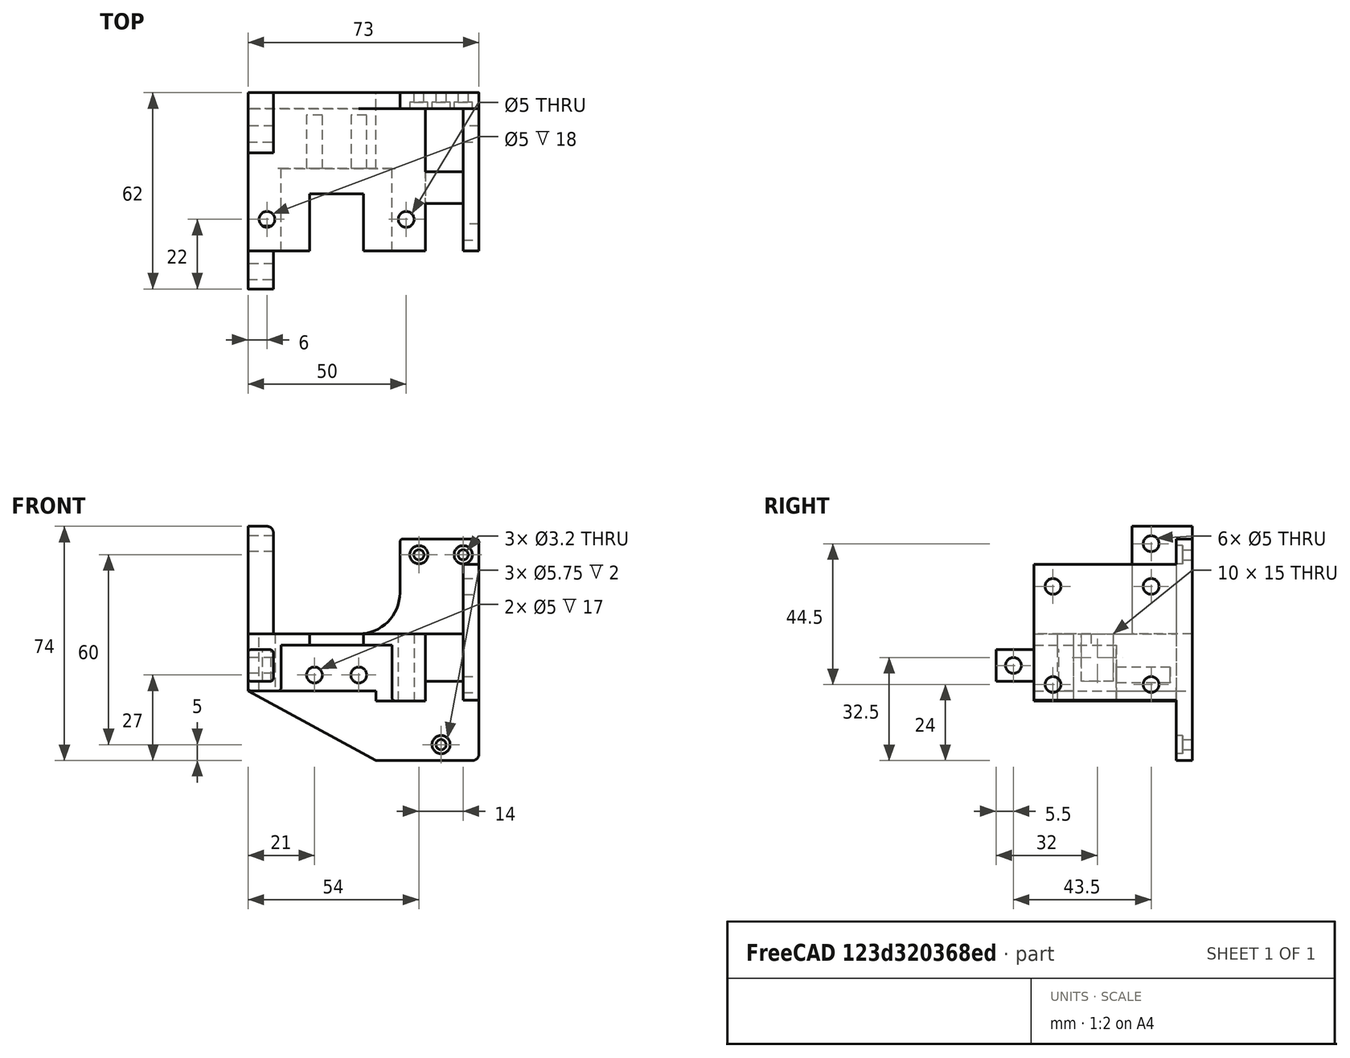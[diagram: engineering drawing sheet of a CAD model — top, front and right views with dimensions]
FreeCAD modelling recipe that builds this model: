
FCSTD DOCUMENT  (FreeCAD 0.19R)
Label: head
License: All rights reserved
LicenseURL: http://en.wikipedia.org/wiki/All_rights_reserved
objects: Sketcher::SketchObject×17, PartDesign::Pocket×13, PartDesign::Fillet×9, PartDesign::Pad×4, PartDesign::Body×1, Mesh::Feature×1
note: 70 computed .brp shape members not serialized (recipe doc carries the construction recipe); baked Part::Feature solids carry a one-line shape summary decoded from their .brp

FEATURE [Sketcher::SketchObject] Sketch
  FullyConstrained = true
  MapMode = 5
  Support = -> [XY_Plane]
  sketch-geometry (5):
    g0: LineSegment StartX=0 StartY=0 StartZ=0 EndX=45 EndY=0 EndZ=0
    g1: LineSegment StartX=-28 StartY=0 StartZ=0 EndX=0 EndY=0 EndZ=0
    g2: LineSegment StartX=-28 StartY=0 StartZ=0 EndX=-28 EndY=-50 EndZ=0
    g3: LineSegment StartX=-28 StartY=-50 StartZ=0 EndX=45 EndY=-50 EndZ=0
    g4: LineSegment StartX=45 StartY=-50 StartZ=0 EndX=45 EndY=0 EndZ=0
  constraints (14):
    c: Coincident(g-1,g0)
    c: PointOnObject(g0,g-1)
    c: PointOnObject(g1,g-1)
    c: Coincident(g1,g0)
    c: Coincident(g1,g2)
    c: Vertical(g2)
    c: Coincident(g2,g3)
    c: Horizontal(g3)
    c: Coincident(g3,g4)
    c: Coincident(g4,g0)
    c: Vertical(g4)
    c: Distance(g4) = 50
    c: DistanceX(g0) = 45
    c: DistanceX(g1) = -28
FEATURE [PartDesign::Pad] Pad
  Direction = (1,1,1)
  Length = 70
  Length2 = 100
  Profile = -> Sketch
  Type = 0
FEATURE [Sketcher::SketchObject] Sketch001
  FullyConstrained = false
  MapMode = 5
  Placement = pos=(0,0,70) rot=(0,0,1;0rad)
  Support = -> [Pad]
  sketch-geometry (4):
    g0: LineSegment StartX=28.1122 StartY=-5 StartZ=0 EndX=40 EndY=-5 EndZ=0
    g1: LineSegment StartX=40 StartY=-5 StartZ=0 EndX=40 EndY=-51.78 EndZ=0
    g2: LineSegment StartX=40 StartY=-51.78 StartZ=0 EndX=28.1122 EndY=-51.78 EndZ=0
    g3: LineSegment StartX=28.1122 StartY=-51.78 StartZ=0 EndX=28.1122 EndY=-5 EndZ=0
  constraints (11):
    c: Coincident(g0,g1)
    c: Coincident(g1,g2)
    c: Coincident(g2,g3)
    c: Coincident(g3,g0)
    c: Horizontal(g0)
    c: Horizontal(g2)
    c: Vertical(g1)
    c: Vertical(g3)
    c: DistanceX(g0) = 40
    c: DistanceY(g1) = -51.78
    c: DistanceY(g0) = -5
FEATURE [PartDesign::Pocket] Pocket  label="BOBnotch"
  BaseFeature = -> Pad
  Length = 5
  Length2 = 100
  Profile = -> Sketch001
  Type = 1
FEATURE [Sketcher::SketchObject] Sketch002
  FullyConstrained = false
  MapMode = 5
  Placement = pos=(0,0,70) rot=(0,0,1;0rad)
  Support = -> [Pocket]
  sketch-geometry (6):
    g0: LineSegment StartX=30 StartY=-5 StartZ=0 EndX=30 EndY=-65.096 EndZ=0
    g1: LineSegment StartX=30 StartY=-65.096 StartZ=0 EndX=-40.7834 EndY=-65.096 EndZ=0
    g2: LineSegment StartX=-40.7834 StartY=-65.096 StartZ=0 EndX=-40.7834 EndY=12.9948 EndZ=0
    g3: LineSegment StartX=-40.7834 StartY=12.9948 StartZ=0 EndX=20 EndY=12.9948 EndZ=0
    g4: LineSegment StartX=20 StartY=12.9948 StartZ=0 EndX=20 EndY=-5 EndZ=0
    g5: LineSegment StartX=20 StartY=-5 StartZ=0 EndX=30 EndY=-5 EndZ=0
  constraints (15):
    c: Coincident(g0,g1)
    c: Coincident(g1,g2)
    c: Horizontal(g1)
    c: Vertical(g0)
    c: Vertical(g2)
    c: DistanceX(g0) = 30
    c: DistanceY(g0) = -5
    c: Coincident(g2,g3)
    c: Horizontal(g3)
    c: Coincident(g3,g4)
    c: Coincident(g4,g5)
    c: Coincident(g5,g0)
    c: Horizontal(g5)
    c: Vertical(g4)
    c: DistanceX(g3) = 20
FEATURE [PartDesign::Pocket] Pocket001  label="stepperplatform"
  BaseFeature = -> Pocket
  Length = 30
  Length2 = 100
  Profile = -> Sketch002
  Type = 0
FEATURE [Sketcher::SketchObject] Sketch003
  FullyConstrained = true
  MapMode = 5
  Placement = pos=(0,0,40) rot=(0,0,1;0rad)
  Support = -> [Pocket001]
  sketch-geometry (2):
    g0: Circle CenterX=-22 CenterY=-40 CenterZ=0 NormalX=0 NormalY=0 NormalZ=1 AngleXU=0 Radius=2.5
    g1: Circle CenterX=22 CenterY=-40 CenterZ=0 NormalX=0 NormalY=0 NormalZ=1 AngleXU=0 Radius=2.5
  constraints (5):
    c: Radius(g1) = 2.5
    c: Equal(g1,g0)
    c: Symmetric(g1,g0,g-2)
    c: Distance(g1,g0) = 44
    c: DistanceY(g0) = -40
FEATURE [PartDesign::Pocket] Pocket002  label="steppermountholes"
  BaseFeature = -> Pocket001
  Length = 5
  Length2 = 100
  Profile = -> Sketch003
  Type = 1
FEATURE [Sketcher::SketchObject] Sketch004
  FullyConstrained = false
  MapMode = 5
  Placement = pos=(0,0,40) rot=(0,0,1;0rad)
  Support = -> [Pocket002]
  sketch-geometry (4):
    g0: LineSegment StartX=-8.5 StartY=-32 StartZ=0 EndX=8.5 EndY=-32 EndZ=0
    g1: LineSegment StartX=8.5 StartY=-32 StartZ=0 EndX=8.5 EndY=-55.3144 EndZ=0
    g2: LineSegment StartX=8.5 StartY=-55.3144 StartZ=0 EndX=-8.5 EndY=-55.3144 EndZ=0
    g3: LineSegment StartX=-8.5 StartY=-55.3144 StartZ=0 EndX=-8.5 EndY=-32 EndZ=0
  constraints (10):
    c: Coincident(g0,g1)
    c: Coincident(g1,g2)
    c: Coincident(g2,g3)
    c: Coincident(g3,g0)
    c: Horizontal(g2)
    c: Vertical(g1)
    c: Vertical(g3)
    c: Symmetric(g0,g0,g-2)
    c: DistanceY(g0) = -32
    c: Distance(g0) = 17
FEATURE [PartDesign::Pocket] Pocket003  label="hotendnotch001"
  BaseFeature = -> Pocket002
  Length = 5
  Length2 = 100
  Profile = -> Sketch004
  Type = 1
FEATURE [Sketcher::SketchObject] Sketch005
  FullyConstrained = false
  MapMode = 5
  Placement = pos=(0,-50,0) rot=(1,0,0;1.5708rad)
  Support = -> [Pocket003]
  sketch-geometry (4):
    g0: LineSegment StartX=-17.5 StartY=36.5 StartZ=0 EndX=17.5 EndY=36.5 EndZ=0
    g1: LineSegment StartX=17.5 StartY=36.5 StartZ=0 EndX=17.5 EndY=-21.4748 EndZ=0
    g2: LineSegment StartX=17.5 StartY=-21.4748 StartZ=0 EndX=-17.5 EndY=-21.4748 EndZ=0
    g3: LineSegment StartX=-17.5 StartY=-21.4748 StartZ=0 EndX=-17.5 EndY=36.5 EndZ=0
  constraints (10):
    c: Coincident(g0,g1)
    c: Coincident(g1,g2)
    c: Coincident(g2,g3)
    c: Coincident(g3,g0)
    c: Horizontal(g2)
    c: Vertical(g1)
    c: Vertical(g3)
    c: Symmetric(g0,g0,g-2)
    c: Distance(g0) = 35
    c: DistanceY(g0) = 36.5
FEATURE [PartDesign::Pocket] Pocket004  label="hotendnotch"
  BaseFeature = -> Pocket003
  Length = 26
  Length2 = 100
  Profile = -> Sketch005
  Type = 0
FEATURE [Sketcher::SketchObject] Sketch006
  FullyConstrained = false
  MapMode = 5
  Placement = pos=(0,-24,5.9e-15) rot=(1,0,0;1.5708rad)
  Support = -> [Pocket004]
  sketch-geometry (4):
    g0: LineSegment StartX=-32.7556 StartY=22 StartZ=0 EndX=12.5 EndY=22 EndZ=0
    g1: LineSegment StartX=12.5 StartY=22 StartZ=0 EndX=12.5 EndY=-8.42821 EndZ=0
    g2: LineSegment StartX=12.5 StartY=-8.42821 StartZ=0 EndX=-32.7556 EndY=-8.42821 EndZ=0
    g3: LineSegment StartX=-32.7556 StartY=-8.42821 StartZ=0 EndX=-32.7556 EndY=22 EndZ=0
  constraints (10):
    c: Coincident(g0,g1)
    c: Coincident(g1,g2)
    c: Coincident(g2,g3)
    c: Coincident(g3,g0)
    c: Horizontal(g0)
    c: Horizontal(g2)
    c: Vertical(g1)
    c: Vertical(g3)
    c: DistanceY(g0) = 22
    c: DistanceX(g0) = 12.5
FEATURE [PartDesign::Pocket] Pocket005  label="fanclearance"
  BaseFeature = -> Pocket004
  Length = 28
  Length2 = 100
  Profile = -> Sketch006
  Type = 4
FEATURE [Sketcher::SketchObject] Sketch007
  FullyConstrained = false
  MapMode = 5
  Placement = pos=(0,-50,0) rot=(1,0,0;1.5708rad)
  Support = -> [Pocket005]
  sketch-geometry (4):
    g0: LineSegment StartX=7.61208 StartY=18.8386 StartZ=0 EndX=33.8542 EndY=18.8386 EndZ=0
    g1: LineSegment StartX=33.8542 StartY=18.8386 StartZ=0 EndX=33.8542 EndY=-10.9025 EndZ=0
    g2: LineSegment StartX=33.8542 StartY=-10.9025 StartZ=0 EndX=7.61208 EndY=-10.9025 EndZ=0
    g3: LineSegment StartX=7.61208 StartY=-10.9025 StartZ=0 EndX=7.61208 EndY=18.8386 EndZ=0
  constraints (8):
    c: Coincident(g0,g1)
    c: Coincident(g1,g2)
    c: Coincident(g2,g3)
    c: Coincident(g3,g0)
    c: Horizontal(g0)
    c: Horizontal(g2)
    c: Vertical(g1)
    c: Vertical(g3)
FEATURE [PartDesign::Pocket] Pocket006  label="bottomconnectorclearance"
  BaseFeature = -> Pocket005
  Length = 45
  Length2 = 100
  Profile = -> Sketch007
  Type = 0
FEATURE [Sketcher::SketchObject] Sketch008
  FullyConstrained = false
  MapMode = 5
  Placement = pos=(0,-50,0) rot=(1,0,0;1.5708rad)
  Support = -> [Pocket006]
  sketch-geometry (8):
    g0: LineSegment StartX=35.0962 StartY=76.3926 StartZ=0 EndX=50.7218 EndY=76.3926 EndZ=0
    g1: LineSegment StartX=50.7218 StartY=76.3926 StartZ=0 EndX=50.7218 EndY=62 EndZ=0
    g2: LineSegment StartX=50.7218 StartY=62 StartZ=0 EndX=35.0962 EndY=62 EndZ=0
    g3: LineSegment StartX=35.0962 StartY=62 StartZ=0 EndX=35.0962 EndY=76.3926 EndZ=0
    g4: LineSegment StartX=34.0545 StartY=19 StartZ=0 EndX=58.6648 EndY=19 EndZ=0
    g5: LineSegment StartX=58.6648 StartY=19 StartZ=0 EndX=58.6648 EndY=-12.6735 EndZ=0
    g6: LineSegment StartX=58.6648 StartY=-12.6735 StartZ=0 EndX=34.0545 EndY=-12.6735 EndZ=0
    g7: LineSegment StartX=34.0545 StartY=-12.6735 StartZ=0 EndX=34.0545 EndY=19 EndZ=0
  constraints (18):
    c: Coincident(g0,g1)
    c: Coincident(g1,g2)
    c: Coincident(g2,g3)
    c: Coincident(g3,g0)
    c: Horizontal(g0)
    c: Horizontal(g2)
    c: Vertical(g1)
    c: Vertical(g3)
    c: Coincident(g4,g5)
    c: Coincident(g5,g6)
    c: Coincident(g6,g7)
    c: Coincident(g7,g4)
    c: Horizontal(g4)
    c: Horizontal(g6)
    c: Vertical(g5)
    c: Vertical(g7)
    c: DistanceY(g2) = 62
    c: DistanceY(g4) = 19
FEATURE [PartDesign::Pocket] Pocket007  label="BOBnotches"
  BaseFeature = -> Pocket006
  Length = 45
  Length2 = 100
  Profile = -> Sketch008
  Type = 0
FEATURE [Sketcher::SketchObject] Sketch009
  FullyConstrained = true
  MapMode = 5
  Placement = pos=(45,0,0) rot=(0.57735,0.57735,0.57735;2.0944rad)
  Support = -> [Pocket007]
  sketch-geometry (5):
    g0: Circle CenterX=-44 CenterY=55 CenterZ=0 NormalX=0 NormalY=0 NormalZ=1 AngleXU=0 Radius=2.5
    g1: Circle CenterX=-13 CenterY=24 CenterZ=0 NormalX=0 NormalY=0 NormalZ=1 AngleXU=0 Radius=2.5
    g2: LineSegment StartX=-44 StartY=55 StartZ=0 EndX=-13 EndY=24 EndZ=0
    g3: Circle CenterX=-13 CenterY=55 CenterZ=0 NormalX=0 NormalY=0 NormalZ=1 AngleXU=0 Radius=2.5
    g4: Circle CenterX=-44 CenterY=24 CenterZ=0 NormalX=0 NormalY=0 NormalZ=1 AngleXU=0 Radius=2.5
  constraints (14):
    c: Coincident(g2,g0)
    c: Coincident(g2,g1)
    c: Angle(g2) = -0.785398
    c: DistanceX(g1) = -13
    c: DistanceY(g1) = 24
    c: Diameter(g4) = 5
    c: Equal(g4,g0)
    c: Equal(g4,g3)
    c: Equal(g4,g1)
    c: DistanceY(g4,g0) = 31
    c: DistanceX(g0,g3) = 31
    c: DistanceX(g4,g1) = 31
    c: DistanceY(g4) = 24
    c: DistanceY(g1,g3) = 31
FEATURE [PartDesign::Pocket] Pocket008  label="stepperholes"
  BaseFeature = -> Pocket007
  Length = 13
  Length2 = 100
  Profile = -> Sketch009
  Type = 0
FEATURE [Sketcher::SketchObject] Sketch010
  FullyConstrained = true
  MapMode = 5
  Placement = pos=(0,0,0) rot=(0,0.707107,0.707107;3.14159rad)
  Support = -> [Pocket008]
  sketch-geometry (3):
    g0: Circle CenterX=-33 CenterY=5 CenterZ=0 NormalX=0 NormalY=0 NormalZ=1 AngleXU=0 Radius=1.6
    g1: Circle CenterX=-40 CenterY=65 CenterZ=0 NormalX=0 NormalY=0 NormalZ=1 AngleXU=0 Radius=1.6
    g2: Circle CenterX=-26 CenterY=65 CenterZ=0 NormalX=0 NormalY=0 NormalZ=1 AngleXU=0 Radius=1.6
  constraints (9):
    c: Diameter(g0) = 3.2
    c: Equal(g0,g2)
    c: Equal(g0,g1)
    c: DistanceX(g0) = -33
    c: Distance(g1,g2) = 14
    c: DistanceX(g2) = -26
    c: DistanceY(g0) = 5
    c: DistanceY(g2) = 65
    c: DistanceY(g1) = 65
FEATURE [PartDesign::Pocket] Pocket009  label="mountholes"
  BaseFeature = -> Pocket008
  Length = 5
  Length2 = 100
  Profile = -> Sketch010
  Type = 0
FEATURE [Sketcher::SketchObject] Sketch014
  FullyConstrained = true
  MapMode = 5
  Placement = pos=(45,0,0) rot=(0.57735,0.57735,0.57735;2.0944rad)
  Support = -> [Pocket009]
  sketch-geometry (4):
    g0: LineSegment StartX=-35 StartY=40 StartZ=0 EndX=-25 EndY=40 EndZ=0
    g1: LineSegment StartX=-25 StartY=40 StartZ=0 EndX=-25 EndY=25 EndZ=0
    g2: LineSegment StartX=-25 StartY=25 StartZ=0 EndX=-35 EndY=25 EndZ=0
    g3: LineSegment StartX=-35 StartY=25 StartZ=0 EndX=-35 EndY=40 EndZ=0
  constraints (12):
    c: Coincident(g0,g1)
    c: Coincident(g1,g2)
    c: Coincident(g2,g3)
    c: Coincident(g3,g0)
    c: Horizontal(g0)
    c: Horizontal(g2)
    c: Vertical(g1)
    c: Vertical(g3)
    c: Distance(g1) = 15
    c: Distance(g0) = 10
    c: DistanceX(g0) = -25
    c: DistanceY(g1) = 25
FEATURE [PartDesign::Pad] Pad001
  BaseFeature = -> Pocket009
  Direction = (1,1,1)
  Length = 23
  Length2 = 100
  Profile = -> Sketch014
  Reversed = true
  Type = 0
FEATURE [Sketcher::SketchObject] Sketch015
  FullyConstrained = false
  MapMode = 5
  Placement = pos=(-28,0,0) rot=(0.57735,-0.57735,-0.57735;2.0944rad)
  Support = -> [Pad001]
  sketch-geometry (8):
    g0: LineSegment StartX=0 StartY=74 StartZ=0 EndX=19 EndY=74 EndZ=0
    g1: LineSegment StartX=19 StartY=74 StartZ=0 EndX=19 EndY=35.8156 EndZ=0
    g2: LineSegment StartX=19 StartY=35.8156 StartZ=0 EndX=0 EndY=35.8156 EndZ=0
    g3: LineSegment StartX=0 StartY=35.8156 StartZ=0 EndX=0 EndY=74 EndZ=0
    g4: LineSegment StartX=42.1188 StartY=35 StartZ=0 EndX=62 EndY=35 EndZ=0
    g5: LineSegment StartX=62 StartY=35 StartZ=0 EndX=62 EndY=25 EndZ=0
    g6: LineSegment StartX=62 StartY=25 StartZ=0 EndX=42.1188 EndY=25 EndZ=0
    g7: LineSegment StartX=42.1188 StartY=25 StartZ=0 EndX=42.1188 EndY=35 EndZ=0
  constraints (21):
    c: Coincident(g0,g1)
    c: Coincident(g1,g2)
    c: Coincident(g2,g3)
    c: Coincident(g3,g0)
    c: Horizontal(g0)
    c: Horizontal(g2)
    c: Vertical(g1)
    c: Vertical(g3)
    c: Distance(g0) = 19
    c: DistanceY(g0) = 74
    c: Coincident(g4,g5)
    c: Coincident(g5,g6)
    c: Coincident(g6,g7)
    c: Coincident(g7,g4)
    c: Horizontal(g4)
    c: Horizontal(g6)
    c: Vertical(g5)
    c: Vertical(g7)
    c: DistanceX(g4) = 62
    c: DistanceY(g4) = 35
    c: DistanceY(g5) = 25
FEATURE [PartDesign::Pad] Pad002  label="fanbosses"
  BaseFeature = -> Pad001
  Direction = (1,1,1)
  Length = 8
  Length2 = 100
  Profile = -> Sketch015
  Reversed = true
  Type = 0
FEATURE [Sketcher::SketchObject] Sketch011
  FullyConstrained = true
  MapMode = 5
  Placement = pos=(-28,0,0) rot=(0.57735,-0.57735,-0.57735;2.0944rad)
  Support = -> [Pad002]
  sketch-geometry (3):
    g0: Circle CenterX=56.5 CenterY=30 CenterZ=0 NormalX=0 NormalY=0 NormalZ=1 AngleXU=0 Radius=2.5
    g1: Circle CenterX=13 CenterY=68.5 CenterZ=0 NormalX=0 NormalY=0 NormalZ=1 AngleXU=0 Radius=2.5
    g2: GeomPoint X=36 Y=48 Z=0
  constraints (8):
    c: Diameter(g0) = 5
    c: DistanceY(g0) = 30
    c: Diameter(g1) = 5
    c: DistanceX(g1) = 13
    c: DistanceY(g0,g2) = 18
    c: DistanceY(g2,g1) = 20.5
    c: DistanceX(g2,g0) = 20.5
    c: DistanceX(g1,g2) = 23
FEATURE [Sketcher::SketchObject] Sketch013
  ExternalGeometry = -> [Pad002]
  FullyConstrained = true
  MapMode = 5
  Placement = pos=(0,-24,5.9e-15) rot=(1,0,0;1.5708rad)
  Support = -> [Pad002]
  sketch-geometry (2):
    g0: Circle CenterX=-7 CenterY=27 CenterZ=0 NormalX=0 NormalY=0 NormalZ=1 AngleXU=0 Radius=2.5
    g1: Circle CenterX=7 CenterY=27 CenterZ=0 NormalX=0 NormalY=0 NormalZ=1 AngleXU=0 Radius=2.5
  constraints (5):
    c: Symmetric(g1,g0,g-2)
    c: Distance(g1,g0) = 14
    c: Diameter(g1) = 5
    c: Equal(g1,g0)
    c: DistanceY(g1,g-3) = 9.5
FEATURE [PartDesign::Pocket] Pocket010
  BaseFeature = -> Pad002
  Length = 17
  Length2 = 100
  Profile = -> Sketch013
  Type = 0
FEATURE [PartDesign::Pocket] Pocket011
  BaseFeature = -> Pocket010
  Length = 15
  Length2 = 100
  Profile = -> Sketch011
  Type = 0
FEATURE [Sketcher::SketchObject] Sketch016
  ExternalGeometry = -> [Pocket011]
  FullyConstrained = false
  MapMode = 5
  Placement = pos=(0,0,0) rot=(0,0.707107,0.707107;3.14159rad)
  Support = -> [Pocket011]
  sketch-geometry (3):
    g0: LineSegment StartX=-12.5 StartY=0 StartZ=0 EndX=28 EndY=22 EndZ=0
    g1: LineSegment StartX=28 StartY=22 StartZ=0 EndX=-20.7119 EndY=22 EndZ=0
    g2: LineSegment StartX=-20.7119 StartY=22 StartZ=0 EndX=-12.5 EndY=0 EndZ=0
  constraints (6):
    c: Coincident(g0,g1)
    c: Horizontal(g1)
    c: Coincident(g1,g2)
    c: Coincident(g2,g0)
    c: Coincident(g0,g-3)
    c: Coincident(g0,g-4)
FEATURE [PartDesign::Pad] Pad003
  BaseFeature = -> Pocket011
  Direction = (1,1,1)
  Length = 5
  Length2 = 100
  Profile = -> Sketch016
  Reversed = true
  Type = 0
FEATURE [PartDesign::Fillet] Fillet
  Base = -> Pad003 [Edge44]
  BaseFeature = -> Pad003
  Radius = 13
  SupportTransform = false
FEATURE [PartDesign::Fillet] Fillet001
  Base = -> Fillet [Edge46]
  BaseFeature = -> Fillet
  Radius = 2
  SupportTransform = false
FEATURE [PartDesign::Fillet] Fillet002
  Base = -> Fillet001 [Edge19]
  BaseFeature = -> Fillet001
  Radius = 1
  SupportTransform = false
FEATURE [PartDesign::Fillet] Fillet003
  Base = -> Fillet002 [Edge38]
  BaseFeature = -> Fillet002
  Radius = 1
  SupportTransform = false
FEATURE [PartDesign::Fillet] Fillet004
  Base = -> Fillet003 [Edge137]
  BaseFeature = -> Fillet003
  Radius = 1
  SupportTransform = false
FEATURE [PartDesign::Fillet] Fillet005
  Base = -> Fillet004 [Edge143]
  BaseFeature = -> Fillet004
  Radius = 1
  SupportTransform = false
FEATURE [PartDesign::Fillet] Fillet006
  Base = -> Fillet005 [Edge137]
  BaseFeature = -> Fillet005
  Radius = 1
  SupportTransform = false
FEATURE [PartDesign::Fillet] Fillet007
  Base = -> Fillet006 [Edge170]
  BaseFeature = -> Fillet006
  Radius = 2
  SupportTransform = false
FEATURE [PartDesign::Fillet] Fillet008
  Base = -> Fillet007 [Edge193,Edge195,Edge192,Edge198]
  BaseFeature = -> Fillet007
  Radius = 1
  SupportTransform = false
FEATURE [Sketcher::SketchObject] Sketch017
  ExternalGeometry = -> [Fillet008]
  FullyConstrained = true
  MapMode = 5
  Placement = pos=(0,-5,0) rot=(1,0,0;1.5708rad)
  Support = -> [Fillet008]
  sketch-geometry (3):
    g0: Circle CenterX=26 CenterY=65 CenterZ=0 NormalX=0 NormalY=0 NormalZ=1 AngleXU=0 Radius=2.875
    g1: Circle CenterX=40 CenterY=65 CenterZ=0 NormalX=0 NormalY=0 NormalZ=1 AngleXU=0 Radius=2.875
    g2: Circle CenterX=33 CenterY=5 CenterZ=0 NormalX=0 NormalY=0 NormalZ=1 AngleXU=0 Radius=2.875
  constraints (6):
    c: Diameter(g2) = 5.75
    c: Equal(g2,g1)
    c: Equal(g2,g0)
    c: Coincident(g0,g-4)
    c: Coincident(g1,g-3)
    c: Coincident(g2,g-5)
FEATURE [PartDesign::Pocket] Pocket012
  BaseFeature = -> Fillet008
  Length = 2
  Length2 = 100
  Profile = -> Sketch017
  Type = 0
FEATURE [PartDesign::Body] Body
  Group = -> [Sketch,Pad,Sketch001,Pocket,Sketch002,Pocket001,Sketch003,Pocket002,Sketch004,Pocket003,Sketch005,Pocket004,Sketch006,Pocket005,Sketch007,Pocket006,Sketch008,Pocket007,Sketch009,Pocket008,Sketch010,Pocket009,Sketch011,Sketch013,Sketch014,Pad001,Sketch015,Pad002,Pocket010,Pocket011,Sketch016,Pad003,Fillet,Fillet001,Fillet002,Fillet003,Fillet004,Fillet005,Fillet006,Fillet007,Fillet008,Sketch017,+1 more]
  Origin = -> Origin
  Tip = -> Pocket012
FEATURE [Mesh::Feature] Mesh  label="Pocket012 (Meshed)"
